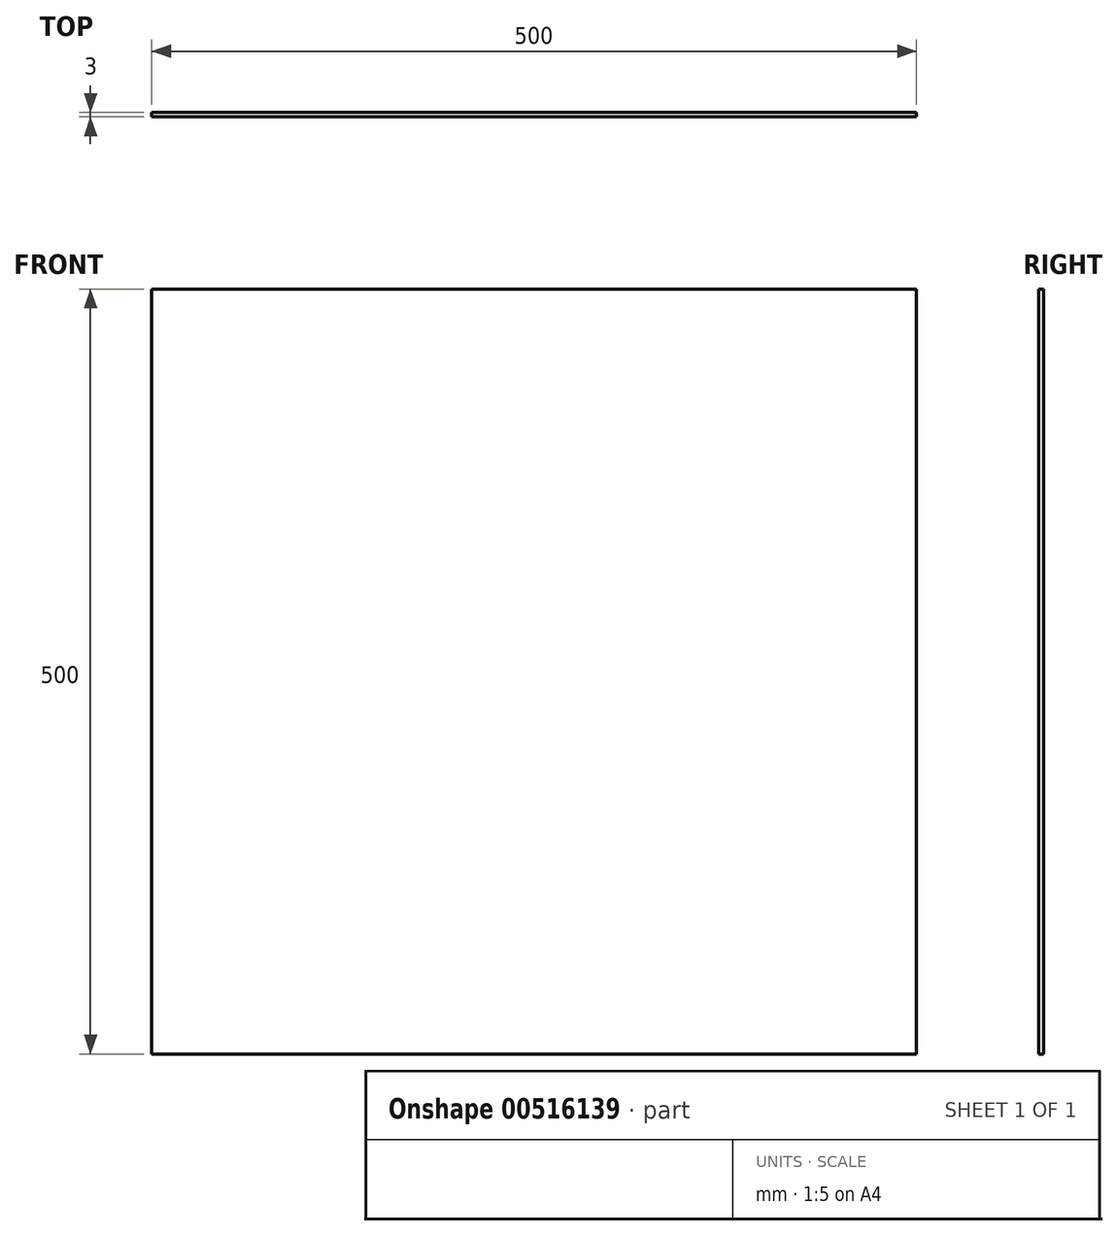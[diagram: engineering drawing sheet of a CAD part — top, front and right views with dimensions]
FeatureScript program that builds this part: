
annotation { "Feature Type Name" : "Feature", "Feature Type Description" : "" }
export const myFeature = defineFeature(function(context is Context, id is Id, definition is map)
    precondition{}
    {
        {
            var Q0;
            Q0=qCreatedBy(makeId("Front.planeOp"),FACE);
            var sketch = newSketch(context, id + "F0", { "sketchPlane" : qUnion([Q0])});
            skLineSegment(sketch, "E0.bottom", {"start": v(250, -250) * mm, "end": v(-250, -250) * mm});
            skLineSegment(sketch, "E0.top", {"start": v(250, 250) * mm, "end": v(-250, 250) * mm});
            skLineSegment(sketch, "E0.left", {"start": v(250, -250) * mm, "end": v(250, 250) * mm});
            skLineSegment(sketch, "E0.right", {"start": v(-250, -250) * mm, "end": v(-250, 250) * mm});
            skPoint(sketch, "E0.middle", {"position": v(0, 0) * mm});
            skSolve(sketch);
        }
        {
            var Q0;
            Q0=makeQuery(id+"F0.imprint","IMPRINT",FACE,{"disambiguationData":[TD([[makeQuery(id+"F0.imprint","IMPRINT",EDGE,{"derivedFrom":sQuery(id+"F0.wireOp",EDGE,"E0.bottom")}),-1.0]])]});
            extrude(context, id + "F1", {"entities" : qUnion([Q0]), "depth" : 3 * mm, "offsetDistance" : 25 * mm});
        }
    });
